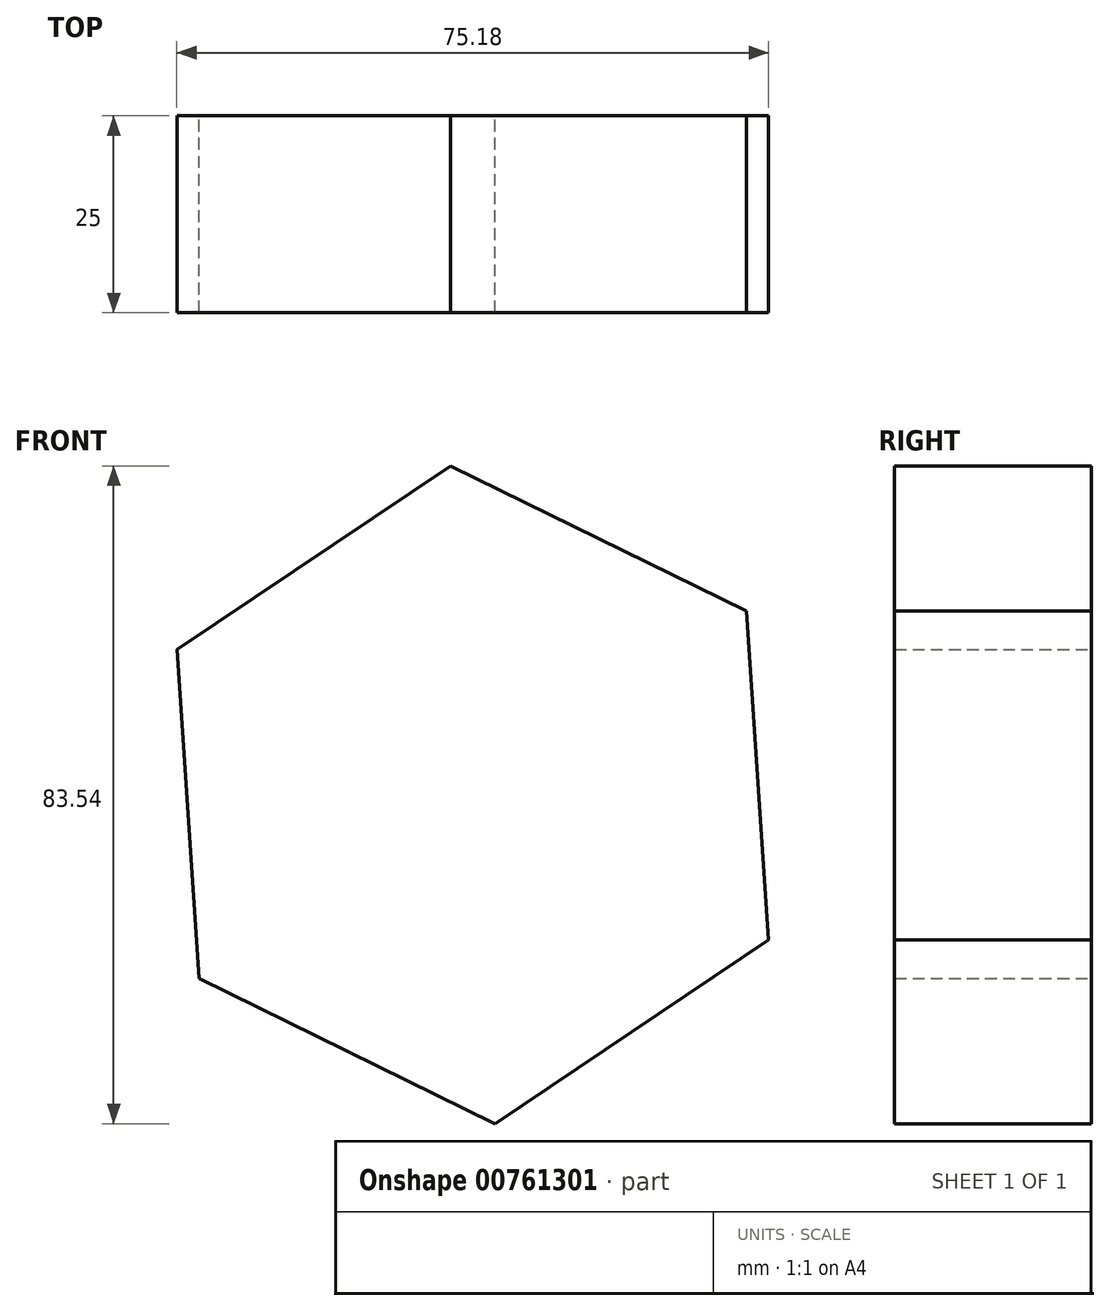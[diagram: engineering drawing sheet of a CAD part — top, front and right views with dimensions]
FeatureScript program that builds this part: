
annotation { "Feature Type Name" : "Feature", "Feature Type Description" : "" }
export const myFeature = defineFeature(function(context is Context, id is Id, definition is map)
    precondition{}
    {
        {
            var Q0;
            Q0=qCreatedBy(makeId("Front.planeOp"),FACE);
            var sketch = newSketch(context, id + "F0", { "sketchPlane" : qUnion([Q0])});
            skCircle(sketch, "E0.cCircle", {"center": v(-91.39, -13.4) * mm, "radius": 36.26 * mm, "construction": true});
            skLineSegment(sketch, "E0.0", {"start": v(-94.21, 28.36) * mm, "end": v(-56.62, 9.93) * mm});
            skLineSegment(sketch, "E0.1", {"start": v(-56.62, 9.93) * mm, "end": v(-53.8, -31.85) * mm});
            skLineSegment(sketch, "E0.2", {"start": v(-53.8, -31.85) * mm, "end": v(-88.56, -55.18) * mm});
            skLineSegment(sketch, "E0.3", {"start": v(-88.56, -55.18) * mm, "end": v(-126.15, -36.74) * mm});
            skLineSegment(sketch, "E0.4", {"start": v(-126.15, -36.74) * mm, "end": v(-128.98, 5.03) * mm});
            skLineSegment(sketch, "E0.5", {"start": v(-128.98, 5.03) * mm, "end": v(-94.21, 28.36) * mm});
            skPoint(sketch, "E0.0.midPoint", {"position": v(-75.42, 19.15) * mm});
            skSolve(sketch);
        }
        {
            var Q0;
            Q0 = qSketchRegion(id + "F0", true);
            extrude(context, id + "F1", {"entities" : qUnion([Q0]), "depth" : 25 * mm, "offsetDistance" : 25 * mm});
        }
    });
